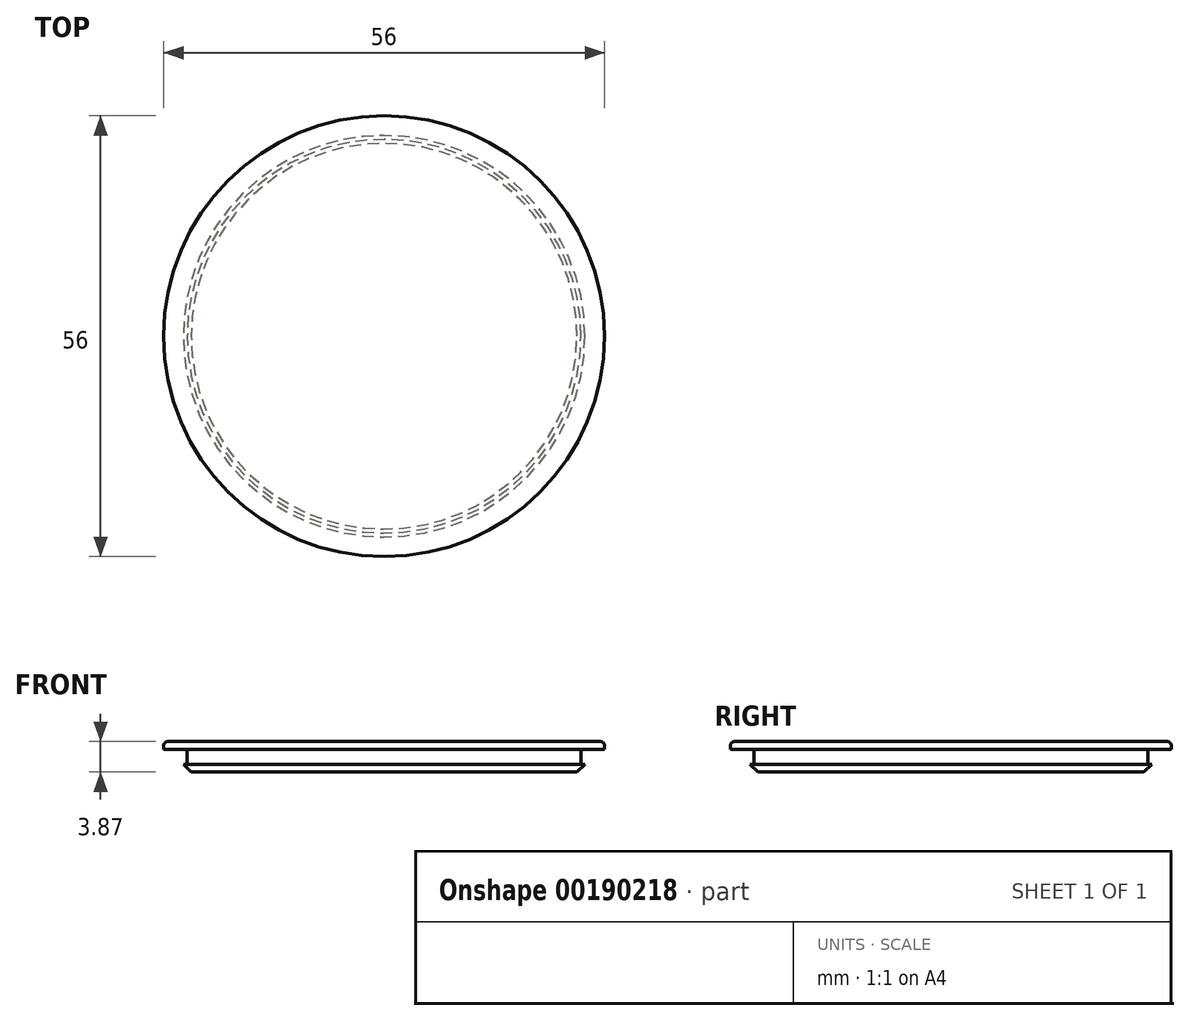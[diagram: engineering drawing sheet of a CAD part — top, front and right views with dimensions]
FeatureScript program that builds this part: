
annotation { "Feature Type Name" : "Feature", "Feature Type Description" : "" }
export const myFeature = defineFeature(function(context is Context, id is Id, definition is map)
    precondition{}
    {
        {
            var Q0;
            Q0=qCreatedBy(makeId("Front.planeOp"),FACE);
            var sketch = newSketch(context, id + "F0", { "sketchPlane" : qUnion([Q0])});
            skLineSegment(sketch, "E0", {"start": v(0, 0) * mm, "end": v(0, 1) * mm});
            skLineSegment(sketch, "E1", {"start": v(0, 1) * mm, "end": v(27.5, 1) * mm});
            skLineSegment(sketch, "E2", {"start": v(28, 0.5) * mm, "end": v(28, 0) * mm});
            skLineSegment(sketch, "E3", {"start": v(28, 0) * mm, "end": v(25.25, 0) * mm});
            skLineSegment(sketch, "E4", {"start": v(25, -0.25) * mm, "end": v(25, -1.87) * mm});
            skLineSegment(sketch, "E5", {"start": v(25, -1.87) * mm, "end": v(25.5, -1.87) * mm});
            skLineSegment(sketch, "E6", {"start": v(25.5, -1.87) * mm, "end": v(24.5, -2.87) * mm});
            skLineSegment(sketch, "E7", {"start": v(24.5, -2.87) * mm, "end": v(0, -2.87) * mm});
            skLineSegment(sketch, "E8", {"start": v(0, -2.87) * mm, "end": v(0, 0) * mm});
            skLineSegment(sketch, "E9", {"start": v(25.5, -1.87) * mm, "end": v(25, -1) * mm});
            skPoint(sketch, "E10.visualSharp", {"position": v(28, 1) * mm});
            skArc(sketch, "E10.filletArc", {"start": v(28, 0.5) * mm, "mid": v(27.85, 0.85) * mm, "end": v(27.5, 1) * mm});
            skPoint(sketch, "E11.visualSharp", {"position": v(25, 0) * mm});
            skArc(sketch, "E11.filletArc", {"start": v(25.25, 0) * mm, "mid": v(25.07, -0.07) * mm, "end": v(25, -0.25) * mm});
            skSolve(sketch);
        }
        {
            var Q0;
            Q0=makeQuery(id+"F0.imprint","IMPRINT",FACE,{"disambiguationData":[TD([[makeQuery(id+"F0.imprint","IMPRINT",EDGE,{"derivedFrom":sQuery(id+"F0.wireOp",EDGE,"E0")}),-1.0]])]});
            var Q1;
            Q1=sQuery(id+"F0.wireOp",EDGE,"E8");
            revolve(context, id + "F1", {"entities" : qUnion([Q0]), "axis" : qUnion([Q1]), "revolveType" : RevolveType.FULL});
        }
    });
